# Revit family: DH
name_source: partatom
category: Wyposażenie mechaniczne
revit_build: Autodesk Revit 2017 (Build: 20160225_1515(x64)
units: mm (PartAtom-declared; Revit-internal decimal feet)

## family parameters
Oparty na płaszczyźnie roboczej = Nie
Punkt obliczania pomieszczeń = Nie
Tnij formami wycięć po wczytaniu = Nie
Typ części = Normalny
Współdzielony = Nie
Wymiar okrągłego złącza = Użyj średnicy
Zawsze pionowo = Tak

## types (30) — shared parameters
Date = 11.2018
Frequency = 50 Hz
Iniet_Collar = Tak
Producent = Rosenberg
Shutter_Automatic = Tak
Socket_Sound_Attenuator = Tak
URL = https://www.rosenberg.pl
Version = 1
t1 = 2 mm  [stored 0.00656168 ft]

## per-type parameters (varying)
| type | A | Air_flow | Current | Da | Di | H | Height | L | P | Power | Pressure | Protection_class | Voltage | W1 | W2 | W3 | Weight[kg] | Width_bottom | Width_top | max.Ambient_temperature |
| 190-2 E.3BE | 294 mm  [stored 0.964567 ft] | 291.0 m³/h | 0 A | 235 mm  [stored 0.770997 ft] | 186 mm  [stored 0.610236 ft] | 600 mm | 140 mm  [stored 0.459318 ft] | 115 mm  [stored 0.377297 ft] | 571 mm  [stored 1.87336 ft] | 0 kW | 199.0 Pa | IP44 | 230 V | 600 mm | 115 mm  [stored 0.377297 ft] | 115 mm  [stored 0.377297 ft] | 3.8 | 335 mm  [stored 1.09908 ft] | 335 mm  [stored 1.09908 ft] | 70 °C |
| 225-2 E.3CF | 294 mm  [stored 0.964567 ft] | 449.0 m³/h | 0 A | 235 mm  [stored 0.770997 ft] | 186 mm  [stored 0.610236 ft] | 600 mm | 140 mm  [stored 0.459318 ft] | 115 mm  [stored 0.377297 ft] | 571 mm  [stored 1.87336 ft] | 0 kW | 218.0 Pa | IP44 | 230 V | 600 mm | 115 mm  [stored 0.377297 ft] | 115 mm  [stored 0.377297 ft] | 5 | 335 mm  [stored 1.09908 ft] | 370 mm  [stored 1.21391 ft] | 70 °C |
| 280-2 E.3EF | 395 mm  [stored 1.29593 ft] | 890.0 m³/h | 1 A | 306 mm  [stored 1.00394 ft] | 256 mm  [stored 0.839895 ft] | 700 mm  [stored 2.29659 ft] | 260 mm  [stored 0.853018 ft] | 156 mm  [stored 0.511811 ft] | 657 mm | 0 kW | 330.0 Pa | IP44 | 230 V | 700 mm  [stored 2.29659 ft] | 156 mm  [stored 0.511811 ft] | 156 mm  [stored 0.511811 ft] | 10.5 | 435 mm  [stored 1.42717 ft] | 550 mm | 70 °C |
| 310-4 E.3EF | 395 mm  [stored 1.29593 ft] | 1031.0 m³/h | 1 A | 306 mm  [stored 1.00394 ft] | 256 mm  [stored 0.839895 ft] | 700 mm  [stored 2.29659 ft] | 260 mm  [stored 0.853018 ft] | 156 mm  [stored 0.511811 ft] | 657 mm | 0 kW | 133.0 Pa | IP44 | 230 V | 700 mm  [stored 2.29659 ft] | 156 mm  [stored 0.511811 ft] | 156 mm  [stored 0.511811 ft] | 10 | 435 mm  [stored 1.42717 ft] | 550 mm | 70 °C |
| 355-4 E.5FA | 555 mm  [stored 1.82087 ft] | 1639.0 m³/h | 1 A | 464 mm  [stored 1.52231 ft] | 402 mm  [stored 1.3189 ft] | 900 mm  [stored 2.95276 ft] | 365 mm  [stored 1.19751 ft] | 220 mm  [stored 0.721785 ft] | 817 mm  [stored 2.68045 ft] | 0 kW | 278.0 Pa | IP54 | 230 V | 900 mm  [stored 2.95276 ft] | 220 mm  [stored 0.721785 ft] | 220 mm  [stored 0.721785 ft] | 23.5 | 595 mm  [stored 1.9521 ft] | 710 mm | 70 °C |
| 400-4 E.5HA | 555 mm  [stored 1.82087 ft] | 2411.0 m³/h | 3 A | 464 mm  [stored 1.52231 ft] | 402 mm  [stored 1.3189 ft] | 900 mm  [stored 2.95276 ft] | 365 mm  [stored 1.19751 ft] | 220 mm  [stored 0.721785 ft] | 817 mm  [stored 2.68045 ft] | 1 kW | 330.0 Pa | IP54 | 230 V | 900 mm  [stored 2.95276 ft] | 220 mm  [stored 0.721785 ft] | 220 mm  [stored 0.721785 ft] | 25.5 | 595 mm  [stored 1.9521 ft] | 710 mm | 65 °C |
| 450-4 E.6FA | 625 mm  [stored 2.05052 ft] | 3436.0 m³/h | 4 A | 464 mm  [stored 1.52231 ft] | 402 mm  [stored 1.3189 ft] | 900 mm  [stored 2.95276 ft] | 440 mm  [stored 1.44357 ft] | 220 mm  [stored 0.721785 ft] | 877 mm  [stored 2.8773 ft] | 1 kW | 450.0 Pa | IP54 | 230 V | 900 mm  [stored 2.95276 ft] | 220 mm  [stored 0.721785 ft] | 220 mm  [stored 0.721785 ft] | 34.8 | 665 mm  [stored 2.18176 ft] | 820 mm  [stored 2.69029 ft] | 45 °C |
| 500-4 E.6HF | 625 mm  [stored 2.05052 ft] | 4745.0 m³/h | 6 A | 464 mm  [stored 1.52231 ft] | 402 mm  [stored 1.3189 ft] | 900 mm  [stored 2.95276 ft] | 450 mm  [stored 1.47638 ft] | 220 mm  [stored 0.721785 ft] | 877 mm  [stored 2.8773 ft] | 1 kW | 509.0 Pa | IP54 | 230 V | 900 mm  [stored 2.95276 ft] | 220 mm  [stored 0.721785 ft] | 220 mm  [stored 0.721785 ft] | 41 | 665 mm  [stored 2.18176 ft] | 900 mm  [stored 2.95276 ft] | 40 °C |
| 560-4 D.6LA | 895 mm  [stored 2.93635 ft] | 6725.0 m³/h | 4 A | 639 mm  [stored 2.09646 ft] | 569 mm  [stored 1.8668 ft] | 1070 mm | 505 mm  [stored 1.65682 ft] | 255 mm  [stored 0.836614 ft] | 1200 mm | 2 kW | 610.0 Pa | IP54 | 400 V | 1070 mm | 255 mm  [stored 0.836614 ft] | 255 mm  [stored 0.836614 ft] | 57 | 939 mm  [stored 3.08071 ft] | 1100 mm | 50 °C |
| 630-4 D.7KF | 895 mm  [stored 2.93635 ft] | 9404.0 m³/h | 6 A | 639 mm  [stored 2.09646 ft] | 569 mm  [stored 1.8668 ft] | 1070 mm | 505 mm  [stored 1.65682 ft] | 255 mm  [stored 0.836614 ft] | 1200 mm | 4 kW | 718.0 Pa | IP54 | 400 V | 1070 mm | 255 mm  [stored 0.836614 ft] | 255 mm  [stored 0.836614 ft] | 81.5 | 939 mm  [stored 3.08071 ft] | 1100 mm | 40 °C |
| 280-4 E.3EF | 395 mm  [stored 1.29593 ft] | 674.0 m³/h | 0 A | 306 mm  [stored 1.00394 ft] | 256 mm  [stored 0.839895 ft] | 700 mm  [stored 2.29659 ft] | 260 mm  [stored 0.853018 ft] | 156 mm  [stored 0.511811 ft] | 657 mm | 0 kW | 129.0 Pa | IP44 | 230 V | 700 mm  [stored 2.29659 ft] | 156 mm  [stored 0.511811 ft] | 156 mm  [stored 0.511811 ft] | 9.5 | 435 mm  [stored 1.42717 ft] | 550 mm | 70 °C |
| 310-4 D.3EF | 395 mm  [stored 1.29593 ft] | 929.0 m³/h | 0 A | 306 mm  [stored 1.00394 ft] | 256 mm  [stored 0.839895 ft] | 700 mm  [stored 2.29659 ft] | 260 mm  [stored 0.853018 ft] | 156 mm  [stored 0.511811 ft] | 657 mm | 0 kW | 117.0 Pa | IP54 | 400 V | 700 mm  [stored 2.29659 ft] | 156 mm  [stored 0.511811 ft] | 156 mm  [stored 0.511811 ft] | 10 | 435 mm  [stored 1.42717 ft] | 550 mm | 70 °C |
| 355-4 D.5DF | 555 mm  [stored 1.82087 ft] | 1639.0 m³/h | 1 A | 464 mm  [stored 1.52231 ft] | 402 mm  [stored 1.3189 ft] | 900 mm  [stored 2.95276 ft] | 365 mm  [stored 1.19751 ft] | 220 mm  [stored 0.721785 ft] | 817 mm  [stored 2.68045 ft] | 0 kW | 266.0 Pa | IP54 | 400 V | 900 mm  [stored 2.95276 ft] | 220 mm  [stored 0.721785 ft] | 220 mm  [stored 0.721785 ft] | 19 | 595 mm  [stored 1.9521 ft] | 710 mm | 70 °C |
| 400-4 D.5FA | 555 mm  [stored 1.82087 ft] | 2470.0 m³/h | 1 A | 464 mm  [stored 1.52231 ft] | 402 mm  [stored 1.3189 ft] | 900 mm  [stored 2.95276 ft] | 365 mm  [stored 1.19751 ft] | 220 mm  [stored 0.721785 ft] | 817 mm  [stored 2.68045 ft] | 0 kW | 299.0 Pa | IP54 | 400 V | 900 mm  [stored 2.95276 ft] | 220 mm  [stored 0.721785 ft] | 220 mm  [stored 0.721785 ft] | 24.5 | 595 mm  [stored 1.9521 ft] | 710 mm | 70 °C |
| 450-4 D.5HA | 625 mm  [stored 2.05052 ft] | 3772.0 m³/h | 2 A | 464 mm  [stored 1.52231 ft] | 402 mm  [stored 1.3189 ft] | 900 mm  [stored 2.95276 ft] | 440 mm  [stored 1.44357 ft] | 220 mm  [stored 0.721785 ft] | 877 mm  [stored 2.8773 ft] | 1 kW | 358.0 Pa | IP54 | 400 V | 900 mm  [stored 2.95276 ft] | 220 mm  [stored 0.721785 ft] | 220 mm  [stored 0.721785 ft] | 30.4 | 665 mm  [stored 2.18176 ft] | 820 mm  [stored 2.69029 ft] | 55 °C |
| 450-6 D.5HA | 625 mm  [stored 2.05052 ft] | 2289.0 m³/h | 1 A | 464 mm  [stored 1.52231 ft] | 402 mm  [stored 1.3189 ft] | 900 mm  [stored 2.95276 ft] | 440 mm  [stored 1.44357 ft] | 220 mm  [stored 0.721785 ft] | 877 mm  [stored 2.8773 ft] | 0 kW | 178.0 Pa | IP54 | 400 V | 900 mm  [stored 2.95276 ft] | 220 mm  [stored 0.721785 ft] | 220 mm  [stored 0.721785 ft] | 30.4 | 665 mm  [stored 2.18176 ft] | 820 mm  [stored 2.69029 ft] | 60 °C |
| 500-4 D.6HF | 625 mm  [stored 2.05052 ft] | 4635.0 m³/h | 3 A | 464 mm  [stored 1.52231 ft] | 402 mm  [stored 1.3189 ft] | 900 mm  [stored 2.95276 ft] | 440 mm  [stored 1.44357 ft] | 220 mm  [stored 0.721785 ft] | 877 mm  [stored 2.8773 ft] | 1 kW | 527.0 Pa | IP54 | 400 V | 900 mm  [stored 2.95276 ft] | 220 mm  [stored 0.721785 ft] | 220 mm  [stored 0.721785 ft] | 40 | 665 mm  [stored 2.18176 ft] | 820 mm  [stored 2.69029 ft] | 70 °C |
| 500-6 D.6DF | 625 mm  [stored 2.05052 ft] | 3114.0 m³/h | 1 A | 464 mm  [stored 1.52231 ft] | 402 mm  [stored 1.3189 ft] | 900 mm  [stored 2.95276 ft] | 440 mm  [stored 1.44357 ft] | 220 mm  [stored 0.721785 ft] | 877 mm  [stored 2.8773 ft] | 0 kW | 221.0 Pa | IP54 | 400 V | 900 mm  [stored 2.95276 ft] | 220 mm  [stored 0.721785 ft] | 220 mm  [stored 0.721785 ft] | 39 | 665 mm  [stored 2.18176 ft] | 820 mm  [stored 2.69029 ft] | 65 °C |
| 560-6 D.6FA | 895 mm  [stored 2.93635 ft] | 4452.0 m³/h | 2 A | 639 mm  [stored 2.09646 ft] | 569 mm  [stored 1.8668 ft] | 1070 mm | 505 mm  [stored 1.65682 ft] | 255 mm  [stored 0.836614 ft] | 1200 mm | 1 kW | 267.0 Pa | IP54 | 400 V | 1070 mm | 255 mm  [stored 0.836614 ft] | 255 mm  [stored 0.836614 ft] | 59 | 939 mm  [stored 3.08071 ft] | 1100 mm | 50 °C |
| 630-6 D.6LA | 895 mm  [stored 2.93635 ft] | 5181.0 m³/h | 3 A | 639 mm  [stored 2.09646 ft] | 569 mm  [stored 1.8668 ft] | 1070 mm | 505 mm  [stored 1.65682 ft] | 255 mm  [stored 0.836614 ft] | 1200 mm | 1 kW | 418.0 Pa | IP54 | 400 V | 1070 mm | 255 mm  [stored 0.836614 ft] | 255 mm  [stored 0.836614 ft] | 74 | 939 mm  [stored 3.08071 ft] | 1100 mm | 65 °C |
| 310 K-4 D Zone 1 | 395 mm  [stored 1.29593 ft] | 929.0 m³/h | 0 A | 306 mm  [stored 1.00394 ft] | 256 mm  [stored 0.839895 ft] | 700 mm  [stored 2.29659 ft] | 260 mm  [stored 0.853018 ft] | 156 mm  [stored 0.511811 ft] | 657 mm | 0 kW | 117.0 Pa | IP44 | 400 V | 700 mm  [stored 2.29659 ft] | 156 mm  [stored 0.511811 ft] | 156 mm  [stored 0.511811 ft] | 13 | 435 mm  [stored 1.42717 ft] | 550 mm | 40 °C |
| 310 L-4 D Zone 1 | 395 mm  [stored 1.29593 ft] | 929.0 m³/h | 0 A | 306 mm  [stored 1.00394 ft] | 256 mm  [stored 0.839895 ft] | 700 mm  [stored 2.29659 ft] | 260 mm  [stored 0.853018 ft] | 156 mm  [stored 0.511811 ft] | 657 mm | 0 kW | 117.0 Pa | IP44 | 400 V | 700 mm  [stored 2.29659 ft] | 156 mm  [stored 0.511811 ft] | 156 mm  [stored 0.511811 ft] | 13 | 435 mm  [stored 1.42717 ft] | 550 mm | 40 °C |
| 355-4 D Zone 1 | 555 mm  [stored 1.82087 ft] | 1639.0 m³/h | 1 A | 464 mm  [stored 1.52231 ft] | 402 mm  [stored 1.3189 ft] | 900 mm  [stored 2.95276 ft] | 365 mm  [stored 1.19751 ft] | 220 mm  [stored 0.721785 ft] | 817 mm  [stored 2.68045 ft] | 0 kW | 266.0 Pa | IP44 | 400 V | 900 mm  [stored 2.95276 ft] | 220 mm  [stored 0.721785 ft] | 220 mm  [stored 0.721785 ft] | 20.5 | 595 mm  [stored 1.9521 ft] | 710 mm | 40 °C |
| 400-4 D Zone 1 | 555 mm  [stored 1.82087 ft] | 2470.0 m³/h | 1 A | 464 mm  [stored 1.52231 ft] | 402 mm  [stored 1.3189 ft] | 900 mm  [stored 2.95276 ft] | 365 mm  [stored 1.19751 ft] | 220 mm  [stored 0.721785 ft] | 817 mm  [stored 2.68045 ft] | 0 kW | 299.0 Pa | IP44 | 400 V | 900 mm  [stored 2.95276 ft] | 220 mm  [stored 0.721785 ft] | 220 mm  [stored 0.721785 ft] | 21.5 | 595 mm  [stored 1.9521 ft] | 710 mm | 40 °C |
| 450-4 D Zone 1 | 625 mm  [stored 2.05052 ft] | 3772.0 m³/h | 1 A | 464 mm  [stored 1.52231 ft] | 402 mm  [stored 1.3189 ft] | 900 mm  [stored 2.95276 ft] | 440 mm  [stored 1.44357 ft] | 220 mm  [stored 0.721785 ft] | 877 mm  [stored 2.8773 ft] | 1 kW | 358.0 Pa | IP54 | 400 V | 900 mm  [stored 2.95276 ft] | 220 mm  [stored 0.721785 ft] | 220 mm  [stored 0.721785 ft] | 30.4 | 665 mm  [stored 2.18176 ft] | 820 mm  [stored 2.69029 ft] | 55 °C |
| 450-6 D Zone 1 | 625 mm  [stored 2.05052 ft] | 3772.0 m³/h | 1 A | 464 mm  [stored 1.52231 ft] | 402 mm  [stored 1.3189 ft] | 900 mm  [stored 2.95276 ft] | 440 mm  [stored 1.44357 ft] | 220 mm  [stored 0.721785 ft] | 877 mm  [stored 2.8773 ft] | 0 kW | 358.0 Pa | IP44 | 400 V | 900 mm  [stored 2.95276 ft] | 220 mm  [stored 0.721785 ft] | 220 mm  [stored 0.721785 ft] | 33 | 665 mm  [stored 2.18176 ft] | 820 mm  [stored 2.69029 ft] | 40 °C |
| 500-4 D Zone 1 | 625 mm  [stored 2.05052 ft] | 4635.0 m³/h | 3 A | 464 mm  [stored 1.52231 ft] | 402 mm  [stored 1.3189 ft] | 900 mm  [stored 2.95276 ft] | 440 mm  [stored 1.44357 ft] | 220 mm  [stored 0.721785 ft] | 877 mm  [stored 2.8773 ft] | 1 kW | 527.0 Pa | IP44 | 400 V | 900 mm  [stored 2.95276 ft] | 220 mm  [stored 0.721785 ft] | 220 mm  [stored 0.721785 ft] | 48 | 665 mm  [stored 2.18176 ft] | 820 mm  [stored 2.69029 ft] | 40 °C |
| 560-4 D Zone 1 | 895 mm  [stored 2.93635 ft] | 6725.0 m³/h | 5 A | 639 mm  [stored 2.09646 ft] | 569 mm  [stored 1.8668 ft] | 1070 mm | 505 mm  [stored 1.65682 ft] | 255 mm  [stored 0.836614 ft] | 1200 mm | 2 kW | 610.0 Pa | IP44 | 400 V | 1070 mm | 255 mm  [stored 0.836614 ft] | 255 mm  [stored 0.836614 ft] | 77.5 | 939 mm  [stored 3.08071 ft] | 1100 mm | 40 °C |
| 560-6 D Zone 1 | 895 mm  [stored 2.93635 ft] | 6725.0 m³/h | 1 A | 639 mm  [stored 2.09646 ft] | 569 mm  [stored 1.8668 ft] | 1070 mm | 505 mm  [stored 1.65682 ft] | 255 mm  [stored 0.836614 ft] | 1200 mm | 1 kW | 610.0 Pa | IP44 | 400 V | 1070 mm | 255 mm  [stored 0.836614 ft] | 255 mm  [stored 0.836614 ft] | 62.5 | 939 mm  [stored 3.08071 ft] | 1100 mm | 40 °C |
| 630-6 D Zone 1 | 895 mm  [stored 2.93635 ft] | 9404.0 m³/h | 2 A | 639 mm  [stored 2.09646 ft] | 569 mm  [stored 1.8668 ft] | 1070 mm | 505 mm  [stored 1.65682 ft] | 255 mm  [stored 0.836614 ft] | 1200 mm | 1 kW | 718.0 Pa | IP44 | 400 V | 1070 mm | 255 mm  [stored 0.836614 ft] | 255 mm  [stored 0.836614 ft] | 67 | 939 mm  [stored 3.08071 ft] | 1100 mm | 40 °C |

note: column(s) folded — value = type name in every type: Model

note: [stored X ft] marks values corroborated as IEEE doubles in the binary element streams (Revit-internal decimal feet)
